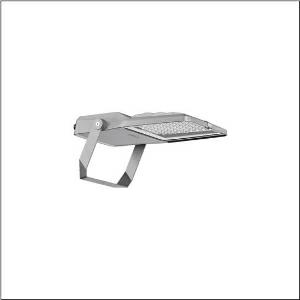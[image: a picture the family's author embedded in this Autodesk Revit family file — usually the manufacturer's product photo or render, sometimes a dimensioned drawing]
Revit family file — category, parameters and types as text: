
# Revit family: floodlight_fl_21_iq_mini___rs12_5xa7772d5b1a_d30b
name_source: partatom
category: Lighting Fixtures
units: mm (PartAtom-declared; Revit-internal decimal feet)

## family parameters
Cut with Voids When Loaded = No
Host = Face
Light Source = No
Part Type = Normal
Room Calculation Point = No
Round Connector Dimension = Use Diameter
Shared = No

## types (1)
- --- (1 x LED, 16820 lm, 143 W, 4000K)
    Apparent Load = 143 VA
    CIE Flux Codes = 79 92 99 100 100
    Color Rendering = 80
    Color Temperature = 4000K
    Default Elevation = 1800 mm
    Description = Floodlight FL 21 iQ mini, floodlight, primary light control with lens, of PMMA, primary optical cover: protective disc, of toughened safety glass, transparent, light distribution: RS12, light emission: direct distribution, installation type: surface-mounted, lamps: LED, High Power LED, rated values: 16.820lm | 143W | 117,6lm/W (begin service life); end service life: 16.820lm | 151,6W; at 50% lumin. flux: 8.410lm | 60,6W | 138,8lm/W, colour temperature: 4000K, colour rendering: CRI > 80, light colour: 840, light setting 1 begin service life: 100% | 16.820lm | 143W | 117,6lm/W | 4.000K, light setting 1 end service life: 151,6W, further light settings possible, control: Street-Remote, Auto-Match, Temp-Guard, Night-Set, Smart-Wire, Desk-Remote (wireless, voltage-free reading and setting of iQ features in the workshop via application-optimized NFC function/RFID function), optimised constant luminous flux control (CLO 2.0), pre-setting: linear dimming characteristic, with terminal, 6-pole, mains connection: 220..240V, AC, 50/60Hz, luminaire housing, of diecast aluminium, powder-coated, SITECO metallic grey (DB 702S), corrosivity category C5 mid according to DIN EN ISO 12944suitable for swimming poolschlorine-resistant, sealing non-destructively replaceable, mounting bracket, of steel, galvanised, powder-coated, SITECO metallic grey (DB 702S), protection rating (complete): IP66, insulation class (complete): insulation class II (safety insulation), certification: CE, ENEC, VDE, protection symbol: D, impact resistance: IK08, permissible operating ambient temperature: -40..+40°C, permissible operating ambient temperature for outdoor applications: -40..+50°C, standard: DIN EN 12944, LABS conformity tested according to VDMA 24364:2018-05, packaging unit: 1 piece

Light Distribution: RS12
    Height = 70 mm
    Lamp = 1 x LED
    Lamp Light Flux = 16820 lm
    Lamp Power = 143 W
    Lamp count = 1
    Length = 485 mm
    Luminous efficacy = 118 lm/W
    Manufacturer = Siteco
    ModVariant = No
    Model = 5XA7772D5B1A
    Number of Poles = 1
    OnlyDefault = Yes
    Power Factor = 1
    Product Name = Floodlight FL 21 iQ mini | RS12
    Product group = floodlight | pylon annexe
    ProductGroupID = 6201
    Protection Class = Protection class II
    Protection Degree = IP 66
    RLX_Detail_Level = 1
    RLX_Emergency_Light_Flux = 0 lm
    RLX_Emergency_Type = 0
    RLX_Emergency_Type_DB = No
    RlxData = <blob elided: 91617 chars, md5=81723560>
    Socket = socket
    Standby Power = 0 W
    System Light Flux = 16820 lm
    System Power = 143 W
    Type Comments = factory setting: luminous flux: 100 % | dim-lin: 254 | 730 mA
    Type Image = l_1006845.jpg
    URL = http://relux.com
    VarID = @adj_166739
    Voltage = 0 V
    Weight = 0.00 kg
    Width = 337 mm

## geometry (parser evidence)
native form markers: Blend x4, Sweep x14
no freeform markers — native parametric forms only
